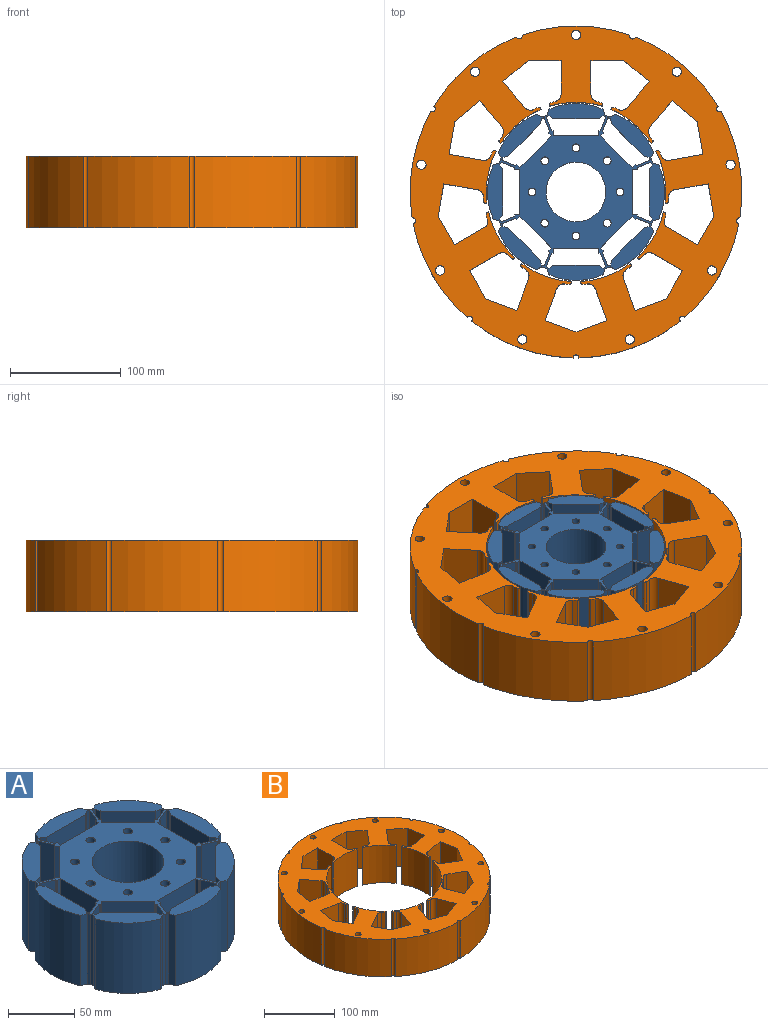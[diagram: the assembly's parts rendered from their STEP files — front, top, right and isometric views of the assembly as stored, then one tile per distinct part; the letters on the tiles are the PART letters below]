
ASSEMBLY  parts=2 mates=1
PART A: 227 faces, bbox 160.1x160.1x65 mm
  f0: cylinder r=3.51mm len=65mm, axis (0,0,1), area 1434.6mm2, adj f201,f202
  f1: cylinder r=3.51mm len=65mm, axis (0,0,1), area 1434.6mm2, adj f201,f202
  f2: cylinder r=3.51mm len=65mm, axis (0,0,1), area 1434.6mm2, adj f201,f202
  f3: cylinder r=3.51mm len=65mm, axis (0,0,1), area 1434.6mm2, adj f201,f202
  f4: cylinder r=3.51mm len=65mm, axis (0,0,1), area 1434.6mm2, adj f201,f202
  f5: cylinder r=3.51mm len=65mm, axis (0,0,1), area 1434.6mm2, adj f201,f202
  f6: cylinder r=3.51mm len=65mm, axis (0,0,1), area 1434.6mm2, adj f201,f202
  f7: cylinder r=3.51mm len=65mm, axis (0,0,1), area 1434.6mm2, adj f201,f202
  f8: cylinder r=27.02mm len=65mm, axis (0,0,1), area 11035.2mm2, adj f201,f202
  f9: cylinder r=0.27mm len=65mm, axis (0,0,1), area 27.6mm2, adj f10,f30,f201,f202
  f10: plane 65x3.78mm, normal (-1,0,0), area 245.9mm2, adj f9,f11,f201,f202
  f11: plane 65x40.67mm, normal (0,1,0), area 2643.2mm2, adj f10,f12,f201,f202
  f12: plane 65x3.78mm, normal (1,0,0), area 245.9mm2, adj f11,f13,f201,f202
  f13: cylinder r=0.27mm len=65mm, axis (0,0,1), area 27.6mm2, adj f12,f14,f201,f202
  f14: plane 65x1.14mm, normal (0,1,0), area 73.9mm2, adj f13,f15,f201,f202
  f15: cylinder r=0.27mm len=65mm, axis (0,0,1), area 20.7mm2, adj f14,f16,f201,f202
  f16: plane 65x11.87mm, normal (0.92,0.38,0), area 835.3mm2, adj f15,f17,f201,f202
  f17: cylinder r=0.27mm len=65mm, axis (0,0,1), area 25.2mm2, adj f16,f18,f201,f202
  f18: cylinder r=53.36mm len=65mm, axis (0,0,1), area 145.8mm2, adj f17,f19,f201,f202
  f19: cylinder r=0.27mm len=65mm, axis (0,0,1), area 19.1mm2, adj f18,f20,f201,f202
  f20: plane 65x3.54mm, normal (-0.57,-0.82,0), area 280mm2, adj f19,f21,f201,f202
  f21: cylinder r=0.27mm len=65mm, axis (0,0,1), area 10.6mm2, adj f20,f22,f201,f202
  f22: plane 65x41.71mm, normal (0,-1,0), area 2711.3mm2, adj f21,f23,f201,f202
  f23: cylinder r=0.27mm len=65mm, axis (0,0,1), area 10.6mm2, adj f22,f24,f201,f202
  f24: plane 65x3.54mm, normal (0.57,-0.82,0), area 280mm2, adj f23,f25,f201,f202
  f25: cylinder r=0.27mm len=65mm, axis (0,0,1), area 19.1mm2, adj f24,f26,f201,f202
  f26: cylinder r=53.36mm len=65mm, axis (0,0,1), area 145.8mm2, adj f25,f27,f201,f202
  f27: cylinder r=0.27mm len=65mm, axis (0,0,1), area 25.2mm2, adj f26,f28,f201,f202
  f28: plane 65x11.87mm, normal (-0.92,0.38,0), area 835.3mm2, adj f27,f29,f201,f202
  f29: cylinder r=0.27mm len=65mm, axis (0,0,1), area 20.7mm2, adj f28,f30,f201,f202
  f30: plane 65x1.14mm, normal (0,1,0), area 73.9mm2, adj f9,f29,f201,f202
  f31: cylinder r=0.27mm len=65mm, axis (0,0,1), area 27.6mm2, adj f32,f52,f201,f202
  f32: plane 65x2.68mm, normal (-0.71,-0.71,0), area 245.9mm2, adj f31,f33,f201,f202
  f33: plane 65x28.75mm, normal (-0.71,0.71,0), area 2643.2mm2, adj f32,f34,f201,f202
  f34: plane 65x2.68mm, normal (0.71,0.71,0), area 245.9mm2, adj f33,f35,f201,f202
  f35: cylinder r=0.27mm len=65mm, axis (0,0,1), area 27.6mm2, adj f34,f36,f201,f202
  f36: plane 65x0.8mm, normal (-0.71,0.71,0), area 73.9mm2, adj f35,f37,f201,f202
  f37: cylinder r=0.27mm len=65mm, axis (0,0,1), area 20.7mm2, adj f36,f38,f201,f202
  f38: plane 65x11.87mm, normal (0.38,0.92,0), area 835.3mm2, adj f37,f39,f201,f202
  f39: cylinder r=0.27mm len=65mm, axis (0,0,1), area 25.2mm2, adj f38,f40,f201,f202
  f40: cylinder r=53.36mm len=65mm, axis (0,0,1), area 145.8mm2, adj f39,f41,f201,f202
  f41: cylinder r=0.27mm len=65mm, axis (0,0,1), area 19.1mm2, adj f40,f42,f201,f202
  f42: plane 65x4.24mm, normal (0.18,-0.98,0), area 280mm2, adj f41,f43,f201,f202
  f43: cylinder r=0.27mm len=65mm, axis (0,0,1), area 10.6mm2, adj f42,f44,f201,f202
  f44: plane 65x29.5mm, normal (0.71,-0.71,0), area 2711.3mm2, adj f43,f45,f201,f202
  f45: cylinder r=0.27mm len=65mm, axis (0,0,1), area 10.6mm2, adj f44,f46,f201,f202
  f46: plane 65x4.24mm, normal (0.98,-0.18,0), area 280mm2, adj f45,f47,f201,f202
  f47: cylinder r=0.27mm len=65mm, axis (0,0,1), area 19.1mm2, adj f46,f48,f201,f202
  f48: cylinder r=53.36mm len=65mm, axis (0,0,1), area 145.8mm2, adj f47,f49,f201,f202
  f49: cylinder r=0.27mm len=65mm, axis (0,0,1), area 25.2mm2, adj f48,f50,f201,f202
  f50: plane 65x11.87mm, normal (-0.92,-0.38,0), area 835.3mm2, adj f49,f51,f201,f202
  f51: cylinder r=0.27mm len=65mm, axis (0,0,1), area 20.7mm2, adj f50,f52,f201,f202
  f52: plane 65x0.8mm, normal (-0.71,0.71,0), area 73.9mm2, adj f31,f51,f201,f202
  f53: cylinder r=0.27mm len=65mm, axis (0,0,1), area 27.6mm2, adj f54,f74,f201,f202
  f54: plane 65x3.78mm, normal (0,-1,0), area 245.9mm2, adj f53,f55,f201,f202
  f55: plane 65x40.67mm, normal (-1,0,0), area 2643.2mm2, adj f54,f56,f201,f202
  f56: plane 65x3.78mm, normal (0,1,0), area 245.9mm2, adj f55,f57,f201,f202
  f57: cylinder r=0.27mm len=65mm, axis (0,0,1), area 27.6mm2, adj f56,f58,f201,f202
  f58: plane 65x1.14mm, normal (-1,0,0), area 73.9mm2, adj f57,f59,f201,f202
  f59: cylinder r=0.27mm len=65mm, axis (0,0,1), area 20.7mm2, adj f58,f60,f201,f202
  f60: plane 65x11.87mm, normal (-0.38,0.92,0), area 835.3mm2, adj f59,f61,f201,f202
  f61: cylinder r=0.27mm len=65mm, axis (0,0,1), area 25.2mm2, adj f60,f62,f201,f202
  f62: cylinder r=53.36mm len=65mm, axis (0,0,1), area 145.8mm2, adj f61,f63,f201,f202
  f63: cylinder r=0.27mm len=65mm, axis (0,0,1), area 19.1mm2, adj f62,f64,f201,f202
  f64: plane 65x3.54mm, normal (0.82,-0.57,0), area 280mm2, adj f63,f65,f201,f202
  f65: cylinder r=0.27mm len=65mm, axis (0,0,1), area 10.6mm2, adj f64,f66,f201,f202
  f66: plane 65x41.71mm, normal (1,0,0), area 2711.3mm2, adj f65,f67,f201,f202
  f67: cylinder r=0.27mm len=65mm, axis (0,0,1), area 10.6mm2, adj f66,f68,f201,f202
  f68: plane 65x3.54mm, normal (0.82,0.57,0), area 280mm2, adj f67,f69,f201,f202
  f69: cylinder r=0.27mm len=65mm, axis (0,0,1), area 19.1mm2, adj f68,f70,f201,f202
  f70: cylinder r=53.36mm len=65mm, axis (0,0,1), area 145.8mm2, adj f69,f71,f201,f202
  f71: cylinder r=0.27mm len=65mm, axis (0,0,1), area 25.2mm2, adj f70,f72,f201,f202
  f72: plane 65x11.87mm, normal (-0.38,-0.92,0), area 835.3mm2, adj f71,f73,f201,f202
  f73: cylinder r=0.27mm len=65mm, axis (0,0,1), area 20.7mm2, adj f72,f74,f201,f202
  f74: plane 65x1.14mm, normal (-1,0,0), area 73.9mm2, adj f53,f73,f201,f202
  f75: cylinder r=0.27mm len=65mm, axis (0,0,1), area 27.6mm2, adj f76,f96,f201,f202
  f76: plane 65x2.68mm, normal (0.71,-0.71,0), area 245.9mm2, adj f75,f77,f201,f202
  f77: plane 65x28.75mm, normal (-0.71,-0.71,0), area 2643.2mm2, adj f76,f78,f201,f202
  f78: plane 65x2.68mm, normal (-0.71,0.71,0), area 245.9mm2, adj f77,f79,f201,f202
  f79: cylinder r=0.27mm len=65mm, axis (0,0,1), area 27.6mm2, adj f78,f80,f201,f202
  f80: plane 65x0.8mm, normal (-0.71,-0.71,0), area 73.9mm2, adj f79,f81,f201,f202
  f81: cylinder r=0.27mm len=65mm, axis (0,0,1), area 20.7mm2, adj f80,f82,f201,f202
  f82: plane 65x11.87mm, normal (-0.92,0.38,0), area 835.3mm2, adj f81,f83,f201,f202
  f83: cylinder r=0.27mm len=65mm, axis (0,0,1), area 25.2mm2, adj f82,f84,f201,f202
  f84: cylinder r=53.36mm len=65mm, axis (0,0,1), area 145.8mm2, adj f83,f85,f201,f202
  f85: cylinder r=0.27mm len=65mm, axis (0,0,1), area 19.1mm2, adj f84,f86,f201,f202
  f86: plane 65x4.24mm, normal (0.98,0.18,0), area 280mm2, adj f85,f87,f201,f202
  f87: cylinder r=0.27mm len=65mm, axis (0,0,1), area 10.6mm2, adj f86,f88,f201,f202
  f88: plane 65x29.5mm, normal (0.71,0.71,0), area 2711.3mm2, adj f87,f89,f201,f202
  f89: cylinder r=0.27mm len=65mm, axis (0,0,1), area 10.6mm2, adj f88,f90,f201,f202
  f90: plane 65x4.24mm, normal (0.18,0.98,0), area 280mm2, adj f89,f91,f201,f202
  f91: cylinder r=0.27mm len=65mm, axis (0,0,1), area 19.1mm2, adj f90,f92,f201,f202
  f92: cylinder r=53.36mm len=65mm, axis (0,0,1), area 145.8mm2, adj f91,f93,f201,f202
  f93: cylinder r=0.27mm len=65mm, axis (0,0,1), area 25.2mm2, adj f92,f94,f201,f202
  f94: plane 65x11.87mm, normal (0.38,-0.92,0), area 835.3mm2, adj f93,f95,f201,f202
  f95: cylinder r=0.27mm len=65mm, axis (0,0,1), area 20.7mm2, adj f94,f96,f201,f202
  f96: plane 65x0.8mm, normal (-0.71,-0.71,0), area 73.9mm2, adj f75,f95,f201,f202
  f97: cylinder r=0.27mm len=65mm, axis (0,0,1), area 27.6mm2, adj f98,f118,f201,f202
  f98: plane 65x3.78mm, normal (1,0,0), area 245.9mm2, adj f97,f99,f201,f202
  f99: plane 65x40.67mm, normal (0,-1,0), area 2643.2mm2, adj f98,f100,f201,f202
  f100: plane 65x3.78mm, normal (-1,0,0), area 245.9mm2, adj f99,f101,f201,f202
  f101: cylinder r=0.27mm len=65mm, axis (0,0,1), area 27.6mm2, adj f100,f102,f201,f202
  f102: plane 65x1.14mm, normal (0,-1,0), area 73.9mm2, adj f101,f103,f201,f202
  f103: cylinder r=0.27mm len=65mm, axis (0,0,1), area 20.7mm2, adj f102,f104,f201,f202
  f104: plane 65x11.87mm, normal (-0.92,-0.38,0), area 835.3mm2, adj f103,f105,f201,f202
  f105: cylinder r=0.27mm len=65mm, axis (0,0,1), area 25.2mm2, adj f104,f106,f201,f202
  f106: cylinder r=53.36mm len=65mm, axis (0,0,1), area 145.8mm2, adj f105,f107,f201,f202
  f107: cylinder r=0.27mm len=65mm, axis (0,0,1), area 19.1mm2, adj f106,f108,f201,f202
  f108: plane 65x3.54mm, normal (0.57,0.82,0), area 280mm2, adj f107,f109,f201,f202
  f109: cylinder r=0.27mm len=65mm, axis (0,0,1), area 10.6mm2, adj f108,f110,f201,f202
  f110: plane 65x41.71mm, normal (0,1,0), area 2711.3mm2, adj f109,f111,f201,f202
  f111: cylinder r=0.27mm len=65mm, axis (0,0,1), area 10.6mm2, adj f110,f112,f201,f202
  f112: plane 65x3.54mm, normal (-0.57,0.82,0), area 280mm2, adj f111,f113,f201,f202
  f113: cylinder r=0.27mm len=65mm, axis (0,0,1), area 19.1mm2, adj f112,f114,f201,f202
  f114: cylinder r=53.36mm len=65mm, axis (0,0,1), area 145.8mm2, adj f113,f115,f201,f202
  f115: cylinder r=0.27mm len=65mm, axis (0,0,1), area 25.2mm2, adj f114,f116,f201,f202
  f116: plane 65x11.87mm, normal (0.92,-0.38,0), area 835.3mm2, adj f115,f117,f201,f202
  f117: cylinder r=0.27mm len=65mm, axis (0,0,1), area 20.7mm2, adj f116,f118,f201,f202
  f118: plane 65x1.14mm, normal (0,-1,0), area 73.9mm2, adj f97,f117,f201,f202
  f119: cylinder r=0.27mm len=65mm, axis (0,0,1), area 27.6mm2, adj f120,f140,f201,f202
  f120: plane 65x2.68mm, normal (0.71,0.71,0), area 245.9mm2, adj f119,f121,f201,f202
  f121: plane 65x28.75mm, normal (0.71,-0.71,0), area 2643.2mm2, adj f120,f122,f201,f202
  f122: plane 65x2.68mm, normal (-0.71,-0.71,0), area 245.9mm2, adj f121,f123,f201,f202
  f123: cylinder r=0.27mm len=65mm, axis (0,0,1), area 27.6mm2, adj f122,f124,f201,f202
  f124: plane 65x0.8mm, normal (0.71,-0.71,0), area 73.9mm2, adj f123,f125,f201,f202
  f125: cylinder r=0.27mm len=65mm, axis (0,0,1), area 20.7mm2, adj f124,f126,f201,f202
  f126: plane 65x11.87mm, normal (-0.38,-0.92,0), area 835.3mm2, adj f125,f127,f201,f202
  f127: cylinder r=0.27mm len=65mm, axis (0,0,1), area 25.2mm2, adj f126,f128,f201,f202
  f128: cylinder r=53.36mm len=65mm, axis (0,0,1), area 145.8mm2, adj f127,f129,f201,f202
  f129: cylinder r=0.27mm len=65mm, axis (0,0,1), area 19.1mm2, adj f128,f130,f201,f202
  f130: plane 65x4.24mm, normal (-0.18,0.98,0), area 280mm2, adj f129,f131,f201,f202
  f131: cylinder r=0.27mm len=65mm, axis (0,0,1), area 10.6mm2, adj f130,f132,f201,f202
  f132: plane 65x29.5mm, normal (-0.71,0.71,0), area 2711.3mm2, adj f131,f133,f201,f202
  f133: cylinder r=0.27mm len=65mm, axis (0,0,1), area 10.6mm2, adj f132,f134,f201,f202
  f134: plane 65x4.24mm, normal (-0.98,0.18,0), area 280mm2, adj f133,f135,f201,f202
  f135: cylinder r=0.27mm len=65mm, axis (0,0,1), area 19.1mm2, adj f134,f136,f201,f202
  f136: cylinder r=53.36mm len=65mm, axis (0,0,1), area 145.8mm2, adj f135,f137,f201,f202
  f137: cylinder r=0.27mm len=65mm, axis (0,0,1), area 25.2mm2, adj f136,f138,f201,f202
  f138: plane 65x11.87mm, normal (0.92,0.38,0), area 835.3mm2, adj f137,f139,f201,f202
  f139: cylinder r=0.27mm len=65mm, axis (0,0,1), area 20.7mm2, adj f138,f140,f201,f202
  f140: plane 65x0.8mm, normal (0.71,-0.71,0), area 73.9mm2, adj f119,f139,f201,f202
  f141: cylinder r=0.27mm len=65mm, axis (0,0,1), area 27.6mm2, adj f142,f162,f201,f202
  f142: plane 65x3.78mm, normal (0,1,0), area 245.9mm2, adj f141,f143,f201,f202
  f143: plane 65x40.67mm, normal (1,0,0), area 2643.2mm2, adj f142,f144,f201,f202
  f144: plane 65x3.78mm, normal (0,-1,0), area 245.9mm2, adj f143,f145,f201,f202
  f145: cylinder r=0.27mm len=65mm, axis (0,0,1), area 27.6mm2, adj f144,f146,f201,f202
  f146: plane 65x1.14mm, normal (1,0,0), area 73.9mm2, adj f145,f147,f201,f202
  f147: cylinder r=0.27mm len=65mm, axis (0,0,1), area 20.7mm2, adj f146,f148,f201,f202
  f148: plane 65x11.87mm, normal (0.38,-0.92,0), area 835.3mm2, adj f147,f149,f201,f202
  f149: cylinder r=0.27mm len=65mm, axis (0,0,1), area 25.2mm2, adj f148,f150,f201,f202
  f150: cylinder r=53.36mm len=65mm, axis (0,0,1), area 145.8mm2, adj f149,f151,f201,f202
  f151: cylinder r=0.27mm len=65mm, axis (0,0,1), area 19.1mm2, adj f150,f152,f201,f202
  f152: plane 65x3.54mm, normal (-0.82,0.57,0), area 280mm2, adj f151,f153,f201,f202
  f153: cylinder r=0.27mm len=65mm, axis (0,0,1), area 10.6mm2, adj f152,f154,f201,f202
  f154: plane 65x41.71mm, normal (-1,0,0), area 2711.3mm2, adj f153,f155,f201,f202
  f155: cylinder r=0.27mm len=65mm, axis (0,0,1), area 10.6mm2, adj f154,f156,f201,f202
  f156: plane 65x3.54mm, normal (-0.82,-0.57,0), area 280mm2, adj f155,f157,f201,f202
  f157: cylinder r=0.27mm len=65mm, axis (0,0,1), area 19.1mm2, adj f156,f158,f201,f202
  f158: cylinder r=53.36mm len=65mm, axis (0,0,1), area 145.8mm2, adj f157,f159,f201,f202
  f159: cylinder r=0.27mm len=65mm, axis (0,0,1), area 25.2mm2, adj f158,f160,f201,f202
  f160: plane 65x11.87mm, normal (0.38,0.92,0), area 835.3mm2, adj f159,f161,f201,f202
  f161: cylinder r=0.27mm len=65mm, axis (0,0,1), area 20.7mm2, adj f160,f162,f201,f202
  f162: plane 65x1.14mm, normal (1,0,0), area 73.9mm2, adj f141,f161,f201,f202
  f163: cylinder r=0.27mm len=65mm, axis (0,0,1), area 27.6mm2, adj f164,f184,f201,f202
  f164: plane 65x2.68mm, normal (-0.71,0.71,0), area 245.9mm2, adj f163,f165,f201,f202
  f165: plane 65x28.75mm, normal (0.71,0.71,0), area 2643.2mm2, adj f164,f166,f201,f202
  f166: plane 65x2.68mm, normal (0.71,-0.71,0), area 245.9mm2, adj f165,f167,f201,f202
  f167: cylinder r=0.27mm len=65mm, axis (0,0,1), area 27.6mm2, adj f166,f168,f201,f202
  f168: plane 65x0.8mm, normal (0.71,0.71,0), area 73.9mm2, adj f167,f169,f201,f202
  f169: cylinder r=0.27mm len=65mm, axis (0,0,1), area 20.7mm2, adj f168,f170,f201,f202
  f170: plane 65x11.87mm, normal (0.92,-0.38,0), area 835.3mm2, adj f169,f171,f201,f202
  f171: cylinder r=0.27mm len=65mm, axis (0,0,1), area 25.2mm2, adj f170,f172,f201,f202
  f172: cylinder r=53.36mm len=65mm, axis (0,0,1), area 145.8mm2, adj f171,f173,f201,f202
  f173: cylinder r=0.27mm len=65mm, axis (0,0,1), area 19.1mm2, adj f172,f174,f201,f202
  f174: plane 65x4.24mm, normal (-0.98,-0.18,0), area 280mm2, adj f173,f175,f201,f202
  f175: cylinder r=0.27mm len=65mm, axis (0,0,1), area 10.6mm2, adj f174,f176,f201,f202
  f176: plane 65x29.5mm, normal (-0.71,-0.71,0), area 2711.3mm2, adj f175,f177,f201,f202
  f177: cylinder r=0.27mm len=65mm, axis (0,0,1), area 10.6mm2, adj f176,f178,f201,f202
  f178: plane 65x4.24mm, normal (-0.18,-0.98,0), area 280mm2, adj f177,f179,f201,f202
  f179: cylinder r=0.27mm len=65mm, axis (0,0,1), area 19.1mm2, adj f178,f180,f201,f202
  f180: cylinder r=53.36mm len=65mm, axis (0,0,1), area 145.8mm2, adj f179,f181,f201,f202
  f181: cylinder r=0.27mm len=65mm, axis (0,0,1), area 25.2mm2, adj f180,f182,f201,f202
  f182: plane 65x11.87mm, normal (-0.38,0.92,0), area 835.3mm2, adj f181,f183,f201,f202
  f183: cylinder r=0.27mm len=65mm, axis (0,0,1), area 20.7mm2, adj f182,f184,f201,f202
  f184: plane 65x0.8mm, normal (0.71,0.71,0), area 73.9mm2, adj f163,f183,f201,f202
  f185: plane 65x4.92mm, normal (0.95,0.3,0), area 335.7mm2, adj f201,f202,f203,f219
  f186: plane 65x4.59mm, normal (-0.46,0.89,0), area 335.7mm2, adj f201,f202,f204,f226
  f187: plane 65x4.59mm, normal (0.89,-0.46,0), area 335.7mm2, adj f201,f202,f218,f226
  f188: plane 65x4.92mm, normal (0.3,0.95,0), area 335.7mm2, adj f201,f202,f217,f225
  f189: plane 65x4.92mm, normal (0.3,-0.95,0), area 335.7mm2, adj f201,f202,f216,f225
  f190: plane 65x4.59mm, normal (0.89,0.46,0), area 335.7mm2, adj f201,f202,f215,f224
  f191: plane 65x4.59mm, normal (-0.46,-0.89,0), area 335.7mm2, adj f201,f202,f214,f224
  f192: plane 65x4.92mm, normal (0.95,-0.3,0), area 335.7mm2, adj f201,f202,f213,f223
  f193: plane 65x4.92mm, normal (-0.95,-0.3,0), area 335.7mm2, adj f201,f202,f212,f223
  f194: plane 65x4.59mm, normal (0.46,-0.89,0), area 335.7mm2, adj f201,f202,f211,f222
  f195: plane 65x4.59mm, normal (-0.89,0.46,0), area 335.7mm2, adj f201,f202,f210,f222
  f196: plane 65x4.92mm, normal (-0.3,-0.95,0), area 335.7mm2, adj f201,f202,f209,f221
  f197: plane 65x4.92mm, normal (-0.3,0.95,0), area 335.7mm2, adj f201,f202,f208,f221
  f198: plane 65x4.59mm, normal (-0.89,-0.46,0), area 335.7mm2, adj f201,f202,f207,f220
  f199: plane 65x4.59mm, normal (0.46,0.89,0), area 335.7mm2, adj f201,f202,f206,f220
  f200: plane 65x4.92mm, normal (-0.95,0.3,0), area 335.7mm2, adj f201,f202,f205,f219
  f201: plane 160.07x160.07mm, normal (0,0,-1), area 11190.9mm2, adj f0,f1,f2,f3,f4,f5,f6,f7
  f202: plane 160.07x160.07mm, normal (0,0,1), area 11190.9mm2, adj f0,f1,f2,f3,f4,f5,f6,f7
  f203: cylinder r=54.72mm len=65mm, axis (0,0,1), area 171.2mm2, adj f185,f201,f202,f204
  f204: cylinder r=54.72mm len=65mm, axis (0,0,1), area 171.2mm2, adj f186,f201,f202,f203
  f205: cylinder r=54.72mm len=65mm, axis (0,0,1), area 171.2mm2, adj f200,f201,f202,f206
  f206: cylinder r=54.72mm len=65mm, axis (0,0,1), area 171.2mm2, adj f199,f201,f202,f205
  f207: cylinder r=54.72mm len=65mm, axis (0,0,1), area 171.2mm2, adj f198,f201,f202,f208
  f208: cylinder r=54.72mm len=65mm, axis (0,0,1), area 171.2mm2, adj f197,f201,f202,f207
  f209: cylinder r=54.72mm len=65mm, axis (0,0,1), area 171.2mm2, adj f196,f201,f202,f210
  f210: cylinder r=54.72mm len=65mm, axis (0,0,1), area 171.2mm2, adj f195,f201,f202,f209
  f211: cylinder r=54.72mm len=65mm, axis (0,0,1), area 171.2mm2, adj f194,f201,f202,f212
  f212: cylinder r=54.72mm len=65mm, axis (0,0,1), area 171.2mm2, adj f193,f201,f202,f211
  f213: cylinder r=54.72mm len=65mm, axis (0,0,1), area 171.2mm2, adj f192,f201,f202,f214
  f214: cylinder r=54.72mm len=65mm, axis (0,0,1), area 171.2mm2, adj f191,f201,f202,f213
  f215: cylinder r=54.72mm len=65mm, axis (0,0,1), area 171.2mm2, adj f190,f201,f202,f216
  f216: cylinder r=54.72mm len=65mm, axis (0,0,1), area 171.2mm2, adj f189,f201,f202,f215
  f217: cylinder r=54.72mm len=65mm, axis (0,0,1), area 171.2mm2, adj f188,f201,f202,f218
  f218: cylinder r=54.72mm len=65mm, axis (0,0,1), area 171.2mm2, adj f187,f201,f202,f217
  f219: cylinder r=58.42mm len=65mm, axis (0,0,1), area 3285.5mm2, adj f185,f200,f201,f202
  f220: cylinder r=58.42mm len=65mm, axis (0,0,1), area 3285.5mm2, adj f198,f199,f201,f202
  f221: cylinder r=58.42mm len=65mm, axis (0,0,1), area 3285.5mm2, adj f196,f197,f201,f202
  f222: cylinder r=58.42mm len=65mm, axis (0,0,1), area 3285.5mm2, adj f194,f195,f201,f202
  f223: cylinder r=58.42mm len=65mm, axis (0,0,1), area 3285.5mm2, adj f192,f193,f201,f202
  f224: cylinder r=58.42mm len=65mm, axis (0,0,1), area 3285.5mm2, adj f190,f191,f201,f202
  f225: cylinder r=58.42mm len=65mm, axis (0,0,1), area 3285.5mm2, adj f188,f189,f201,f202
  f226: cylinder r=58.42mm len=65mm, axis (0,0,1), area 3285.5mm2, adj f186,f187,f201,f202
PART B: 146 faces, bbox 299.9x299.9x65 mm
  f0: cylinder r=149.96mm len=74.68mm, axis (0,0,1), area 6453.7mm2, adj f1,f17,f144,f145
  f1: cylinder r=2.7mm len=65mm, axis (0,0,1), area 548.6mm2, adj f0,f2,f144,f145
  f2: cylinder r=149.96mm len=96mm, axis (0,0,1), area 6453.7mm2, adj f1,f3,f144,f145
  f3: cylinder r=2.7mm len=65mm, axis (0,0,1), area 548.6mm2, adj f2,f4,f144,f145
  f4: cylinder r=149.96mm len=84.42mm, axis (0,0,1), area 6453.7mm2, adj f3,f5,f144,f145
  f5: cylinder r=2.7mm len=65mm, axis (0,0,1), area 548.6mm2, adj f4,f6,f144,f145
  f6: cylinder r=149.96mm len=91.61mm, axis (0,0,1), area 6453.7mm2, adj f5,f7,f144,f145
  f7: cylinder r=2.7mm len=65mm, axis (0,0,1), area 548.6mm2, adj f6,f8,f144,f145
  f8: cylinder r=149.96mm len=91.61mm, axis (0,0,1), area 6453.7mm2, adj f7,f9,f144,f145
  f9: cylinder r=2.7mm len=65mm, axis (0,0,1), area 551.7mm2, adj f8,f10,f144,f145
  f10: cylinder r=149.96mm len=84.42mm, axis (0,0,1), area 6453.7mm2, adj f9,f11,f144,f145
  f11: cylinder r=2.7mm len=65mm, axis (0,0,1), area 551.7mm2, adj f10,f12,f144,f145
  f12: cylinder r=149.96mm len=96mm, axis (0,0,1), area 6453.7mm2, adj f11,f13,f144,f145
  f13: cylinder r=2.7mm len=65mm, axis (0,0,1), area 551.7mm2, adj f12,f14,f144,f145
  f14: cylinder r=149.96mm len=74.68mm, axis (0,0,1), area 6453.7mm2, adj f13,f15,f144,f145
  f15: cylinder r=2.7mm len=65mm, axis (0,0,1), area 551.7mm2, adj f14,f16,f144,f145
  f16: cylinder r=149.96mm len=97.49mm, axis (0,0,1), area 6453.7mm2, adj f15,f17,f144,f145
  f17: cylinder r=2.7mm len=65mm, axis (0,0,1), area 548.6mm2, adj f0,f16,f144,f145
  f18: cylinder r=4.19mm len=65mm, axis (0,0,1), area 1710.4mm2, adj f144,f145
  f19: cylinder r=4.19mm len=65mm, axis (0,0,1), area 1710.4mm2, adj f144,f145
  f20: cylinder r=4.19mm len=65mm, axis (0,0,1), area 1710.4mm2, adj f144,f145
  f21: cylinder r=4.19mm len=65mm, axis (0,0,1), area 1710.4mm2, adj f144,f145
  f22: cylinder r=4.19mm len=65mm, axis (0,0,1), area 1710.4mm2, adj f144,f145
  f23: cylinder r=4.19mm len=65mm, axis (0,0,1), area 1710.4mm2, adj f144,f145
  f24: cylinder r=4.19mm len=65mm, axis (0,0,1), area 1710.4mm2, adj f144,f145
  f25: cylinder r=4.19mm len=65mm, axis (0,0,1), area 1710.4mm2, adj f144,f145
  f26: cylinder r=4.19mm len=65mm, axis (0,0,1), area 1710.4mm2, adj f144,f145
  f27: plane 65x30.67mm, normal (1,0,0), area 1993.5mm2, adj f28,f143,f144,f145
  f28: plane 65x29.76mm, normal (0,-1,0), area 1934.5mm2, adj f27,f29,f144,f145
  f29: plane 65x22.8mm, normal (-0.64,-0.77,0), area 1934.5mm2, adj f28,f30,f144,f145
  f30: plane 65x23.49mm, normal (-0.77,0.64,0), area 1993.5mm2, adj f29,f31,f144,f145
  f31: cylinder r=6.75mm len=65mm, axis (0,0,1), area 590.6mm2, adj f30,f32,f144,f145
  f32: cylinder r=83.76mm len=65mm, axis (0,0,1), area 285.1mm2, adj f31,f33,f144,f145
  f33: cylinder r=1.76mm len=65mm, axis (0,0,1), area 187.4mm2, adj f32,f34,f144,f145
  f34: plane 65x0.79mm, normal (-0.94,0.34,0), area 54.7mm2, adj f33,f35,f144,f145
  f35: cylinder r=81.06mm len=65mm, axis (0,0,1), area 3151.3mm2, adj f34,f36,f144,f145
  f36: plane 65x0.73mm, normal (0.5,-0.87,0), area 54.7mm2, adj f35,f37,f144,f145
  f37: cylinder r=1.76mm len=65mm, axis (0,0,1), area 187.4mm2, adj f36,f38,f144,f145
  f38: cylinder r=83.76mm len=65mm, axis (0,0,1), area 285.1mm2, adj f37,f39,f144,f145
  f39: cylinder r=6.75mm len=65mm, axis (0,0,1), area 590.6mm2, adj f38,f40,f144,f145
  f40: plane 65x23.49mm, normal (0.77,-0.64,0), area 1993.5mm2, adj f39,f41,f144,f145
  f41: plane 65x22.8mm, normal (-0.64,-0.77,0), area 1934.5mm2, adj f40,f42,f144,f145
  f42: plane 65x29.31mm, normal (-0.98,-0.17,0), area 1934.5mm2, adj f41,f43,f144,f145
  f43: plane 65x30.2mm, normal (-0.17,0.98,0), area 1993.5mm2, adj f42,f44,f144,f145
  f44: cylinder r=6.75mm len=65mm, axis (0,0,1), area 590.6mm2, adj f43,f45,f144,f145
  f45: cylinder r=83.76mm len=65mm, axis (0,0,1), area 285.1mm2, adj f44,f46,f144,f145
  f46: cylinder r=1.76mm len=65mm, axis (0,0,1), area 187.4mm2, adj f45,f47,f144,f145
  f47: plane 65x0.73mm, normal (-0.5,0.87,0), area 54.7mm2, adj f46,f48,f144,f145
  f48: cylinder r=81.06mm len=65mm, axis (0,0,1), area 3151.3mm2, adj f47,f49,f144,f145
  f49: plane 65x0.83mm, normal (-0.17,-0.98,0), area 54.7mm2, adj f48,f50,f144,f145
  f50: cylinder r=1.76mm len=65mm, axis (0,0,1), area 187.4mm2, adj f49,f51,f144,f145
  f51: cylinder r=83.76mm len=65mm, axis (0,0,1), area 285.1mm2, adj f50,f52,f144,f145
  f52: cylinder r=6.75mm len=65mm, axis (0,0,1), area 590.6mm2, adj f51,f53,f144,f145
  f53: plane 65x30.2mm, normal (0.17,-0.98,0), area 1993.5mm2, adj f52,f54,f144,f145
  f54: plane 65x29.31mm, normal (-0.98,-0.17,0), area 1934.5mm2, adj f53,f55,f144,f145
  f55: plane 65x25.77mm, normal (-0.87,0.5,0), area 1934.5mm2, adj f54,f56,f144,f145
  f56: plane 65x26.56mm, normal (0.5,0.87,0), area 1993.5mm2, adj f55,f57,f144,f145
  f57: cylinder r=6.75mm len=65mm, axis (0,0,1), area 590.6mm2, adj f56,f58,f144,f145
  f58: cylinder r=83.76mm len=65mm, axis (0,0,1), area 285.1mm2, adj f57,f59,f144,f145
  f59: cylinder r=1.76mm len=65mm, axis (0,0,1), area 187.4mm2, adj f58,f60,f144,f145
  f60: plane 65x0.83mm, normal (0.17,0.98,0), area 54.7mm2, adj f59,f61,f144,f145
  f61: cylinder r=81.06mm len=65mm, axis (0,0,1), area 3151.3mm2, adj f60,f62,f144,f145
  f62: plane 65x0.64mm, normal (-0.77,-0.64,0), area 54.7mm2, adj f61,f63,f144,f145
  f63: cylinder r=1.76mm len=65mm, axis (0,0,1), area 187.4mm2, adj f62,f64,f144,f145
  f64: cylinder r=83.76mm len=65mm, axis (0,0,1), area 285.1mm2, adj f63,f65,f144,f145
  f65: cylinder r=6.75mm len=65mm, axis (0,0,1), area 590.6mm2, adj f64,f66,f144,f145
  f66: plane 65x26.56mm, normal (-0.5,-0.87,0), area 1993.5mm2, adj f65,f67,f144,f145
  f67: plane 65x25.77mm, normal (-0.87,0.5,0), area 1934.5mm2, adj f66,f68,f144,f145
  f68: plane 65x27.97mm, normal (-0.34,0.94,0), area 1934.5mm2, adj f67,f69,f144,f145
  f69: plane 65x28.82mm, normal (0.94,0.34,0), area 1993.5mm2, adj f68,f70,f144,f145
  f70: cylinder r=6.75mm len=65mm, axis (0,0,1), area 590.6mm2, adj f69,f71,f144,f145
  f71: cylinder r=83.76mm len=65mm, axis (0,0,1), area 285.1mm2, adj f70,f72,f144,f145
  f72: cylinder r=1.76mm len=65mm, axis (0,0,1), area 187.4mm2, adj f71,f73,f144,f145
  f73: plane 65x0.64mm, normal (0.77,0.64,0), area 54.7mm2, adj f72,f74,f144,f145
  f74: cylinder r=81.06mm len=65mm, axis (0,0,1), area 3151.3mm2, adj f73,f75,f144,f145
  f75: plane 65x0.84mm, normal (-1,0,0), area 54.7mm2, adj f74,f76,f144,f145
  f76: cylinder r=1.76mm len=65mm, axis (0,0,1), area 187.4mm2, adj f75,f77,f144,f145
  f77: cylinder r=83.76mm len=65mm, axis (0,0,1), area 285.1mm2, adj f76,f78,f144,f145
  f78: cylinder r=6.75mm len=65mm, axis (0,0,1), area 590.6mm2, adj f77,f79,f144,f145
  f79: plane 65x28.82mm, normal (-0.94,-0.34,0), area 1993.5mm2, adj f78,f80,f144,f145
  f80: plane 65x27.97mm, normal (-0.34,0.94,0), area 1934.5mm2, adj f79,f81,f144,f145
  f81: plane 65x27.97mm, normal (0.34,0.94,0), area 1934.5mm2, adj f80,f82,f144,f145
  f82: plane 65x28.82mm, normal (0.94,-0.34,0), area 1993.5mm2, adj f81,f83,f144,f145
  f83: cylinder r=6.75mm len=65mm, axis (0,0,1), area 590.6mm2, adj f82,f84,f144,f145
  f84: cylinder r=83.76mm len=65mm, axis (0,0,1), area 285.1mm2, adj f83,f85,f144,f145
  f85: cylinder r=1.76mm len=65mm, axis (0,0,1), area 187.4mm2, adj f84,f86,f144,f145
  f86: plane 65x0.84mm, normal (1,0,0), area 54.7mm2, adj f85,f87,f144,f145
  f87: cylinder r=81.06mm len=65mm, axis (0,0,1), area 3151.3mm2, adj f86,f88,f144,f145
  f88: plane 65x0.64mm, normal (-0.77,0.64,0), area 54.7mm2, adj f87,f89,f144,f145
  f89: cylinder r=1.76mm len=65mm, axis (0,0,1), area 187.4mm2, adj f88,f90,f144,f145
  f90: cylinder r=83.76mm len=65mm, axis (0,0,1), area 285.1mm2, adj f89,f91,f144,f145
  f91: cylinder r=6.75mm len=65mm, axis (0,0,1), area 590.6mm2, adj f90,f92,f144,f145
  f92: plane 65x28.82mm, normal (-0.94,0.34,0), area 1993.5mm2, adj f91,f93,f144,f145
  f93: plane 65x27.97mm, normal (0.34,0.94,0), area 1934.5mm2, adj f92,f94,f144,f145
  f94: plane 65x25.77mm, normal (0.87,0.5,0), area 1934.5mm2, adj f93,f95,f144,f145
  f95: plane 65x26.56mm, normal (0.5,-0.87,0), area 1993.5mm2, adj f94,f96,f144,f145
  f96: cylinder r=6.75mm len=65mm, axis (0,0,1), area 590.6mm2, adj f95,f97,f144,f145
  f97: cylinder r=83.76mm len=65mm, axis (0,0,1), area 285.1mm2, adj f96,f98,f144,f145
  f98: cylinder r=1.76mm len=65mm, axis (0,0,1), area 187.4mm2, adj f97,f99,f144,f145
  f99: plane 65x0.64mm, normal (0.77,-0.64,0), area 54.7mm2, adj f98,f100,f144,f145
  f100: cylinder r=81.06mm len=65mm, axis (0,0,1), area 3151.3mm2, adj f99,f101,f144,f145
  f101: plane 65x0.83mm, normal (-0.17,0.98,0), area 54.7mm2, adj f100,f102,f144,f145
  f102: cylinder r=1.76mm len=65mm, axis (0,0,1), area 187.4mm2, adj f101,f103,f144,f145
  f103: cylinder r=83.76mm len=65mm, axis (0,0,1), area 285.1mm2, adj f102,f104,f144,f145
  f104: cylinder r=6.75mm len=65mm, axis (0,0,1), area 590.6mm2, adj f103,f105,f144,f145
  f105: plane 65x26.56mm, normal (-0.5,0.87,0), area 1993.5mm2, adj f104,f106,f144,f145
  f106: plane 65x25.77mm, normal (0.87,0.5,0), area 1934.5mm2, adj f105,f107,f144,f145
  f107: plane 65x29.31mm, normal (0.98,-0.17,0), area 1934.5mm2, adj f106,f108,f144,f145
  f108: plane 65x30.2mm, normal (-0.17,-0.98,0), area 1993.5mm2, adj f107,f109,f144,f145
  f109: cylinder r=6.75mm len=65mm, axis (0,0,1), area 590.6mm2, adj f108,f110,f144,f145
  f110: cylinder r=83.76mm len=65mm, axis (0,0,1), area 285.1mm2, adj f109,f111,f144,f145
  f111: cylinder r=1.76mm len=65mm, axis (0,0,1), area 187.4mm2, adj f110,f112,f144,f145
  f112: plane 65x0.83mm, normal (0.17,-0.98,0), area 54.7mm2, adj f111,f113,f144,f145
  f113: cylinder r=81.06mm len=65mm, axis (0,0,1), area 3151.3mm2, adj f112,f114,f144,f145
  f114: plane 65x0.73mm, normal (0.5,0.87,0), area 54.7mm2, adj f113,f115,f144,f145
  f115: cylinder r=1.76mm len=65mm, axis (0,0,1), area 187.4mm2, adj f114,f116,f144,f145
  f116: cylinder r=83.76mm len=65mm, axis (0,0,1), area 285.1mm2, adj f115,f117,f144,f145
  f117: cylinder r=6.75mm len=65mm, axis (0,0,1), area 590.6mm2, adj f116,f118,f144,f145
  f118: plane 65x30.2mm, normal (0.17,0.98,0), area 1993.5mm2, adj f117,f119,f144,f145
  f119: plane 65x29.31mm, normal (0.98,-0.17,0), area 1934.5mm2, adj f118,f120,f144,f145
  f120: plane 65x22.8mm, normal (0.64,-0.77,0), area 1934.5mm2, adj f119,f121,f144,f145
  f121: plane 65x23.49mm, normal (-0.77,-0.64,0), area 1993.5mm2, adj f120,f122,f144,f145
  f122: cylinder r=6.75mm len=65mm, axis (0,0,1), area 590.6mm2, adj f121,f123,f144,f145
  f123: cylinder r=83.76mm len=65mm, axis (0,0,1), area 285.1mm2, adj f122,f124,f144,f145
  f124: cylinder r=1.76mm len=65mm, axis (0,0,1), area 187.4mm2, adj f123,f125,f144,f145
  f125: plane 65x0.73mm, normal (-0.5,-0.87,0), area 54.7mm2, adj f124,f126,f144,f145
  f126: cylinder r=81.06mm len=65mm, axis (0,0,1), area 3151.3mm2, adj f125,f127,f144,f145
  f127: plane 65x0.79mm, normal (0.94,0.34,0), area 54.7mm2, adj f126,f128,f144,f145
  f128: cylinder r=1.76mm len=65mm, axis (0,0,1), area 187.4mm2, adj f127,f129,f144,f145
  f129: cylinder r=83.76mm len=65mm, axis (0,0,1), area 285.1mm2, adj f128,f130,f144,f145
  f130: cylinder r=6.75mm len=65mm, axis (0,0,1), area 590.6mm2, adj f129,f131,f144,f145
  f131: plane 65x23.49mm, normal (0.77,0.64,0), area 1993.5mm2, adj f130,f132,f144,f145
  f132: plane 65x22.8mm, normal (0.64,-0.77,0), area 1934.5mm2, adj f131,f133,f144,f145
  f133: plane 65x29.76mm, normal (0,-1,0), area 1934.5mm2, adj f132,f134,f144,f145
  f134: plane 65x30.67mm, normal (-1,0,0), area 1993.5mm2, adj f133,f135,f144,f145
  f135: cylinder r=6.75mm len=65mm, axis (0,0,1), area 590.6mm2, adj f134,f136,f144,f145
  f136: cylinder r=83.76mm len=65mm, axis (0,0,1), area 285.1mm2, adj f135,f137,f144,f145
  f137: cylinder r=1.76mm len=65mm, axis (0,0,1), area 187.4mm2, adj f136,f138,f144,f145
  f138: plane 65x0.79mm, normal (-0.94,-0.34,0), area 54.7mm2, adj f137,f139,f144,f145
  f139: cylinder r=81.06mm len=65mm, axis (0,0,1), area 3151.3mm2, adj f138,f140,f144,f145
  f140: plane 65x0.79mm, normal (0.94,-0.34,0), area 54.7mm2, adj f139,f141,f144,f145
  f141: cylinder r=1.76mm len=65mm, axis (0,0,1), area 187.4mm2, adj f140,f142,f144,f145
  f142: cylinder r=83.76mm len=65mm, axis (0,0,1), area 285.1mm2, adj f141,f143,f144,f145
  f143: cylinder r=6.75mm len=65mm, axis (0,0,1), area 590.6mm2, adj f27,f142,f144,f145
  f144: plane 299.92x299.9mm, normal (0,0,1), area 33675.4mm2, adj f0,f1,f2,f3,f4,f5,f6,f7
  f145: plane 299.92x299.9mm, normal (0,0,-1), area 33675.4mm2, adj f0,f1,f2,f3,f4,f5,f6,f7
PLACE A t=(-47.16,-46.41,3.75)mm
PLACE B t=(-47.16,-46.41,3.75)mm
MATE fastened A.f8 <-> B.f0  axis (0,0,1) through (-47.16,-46.41,-61.25)mm
